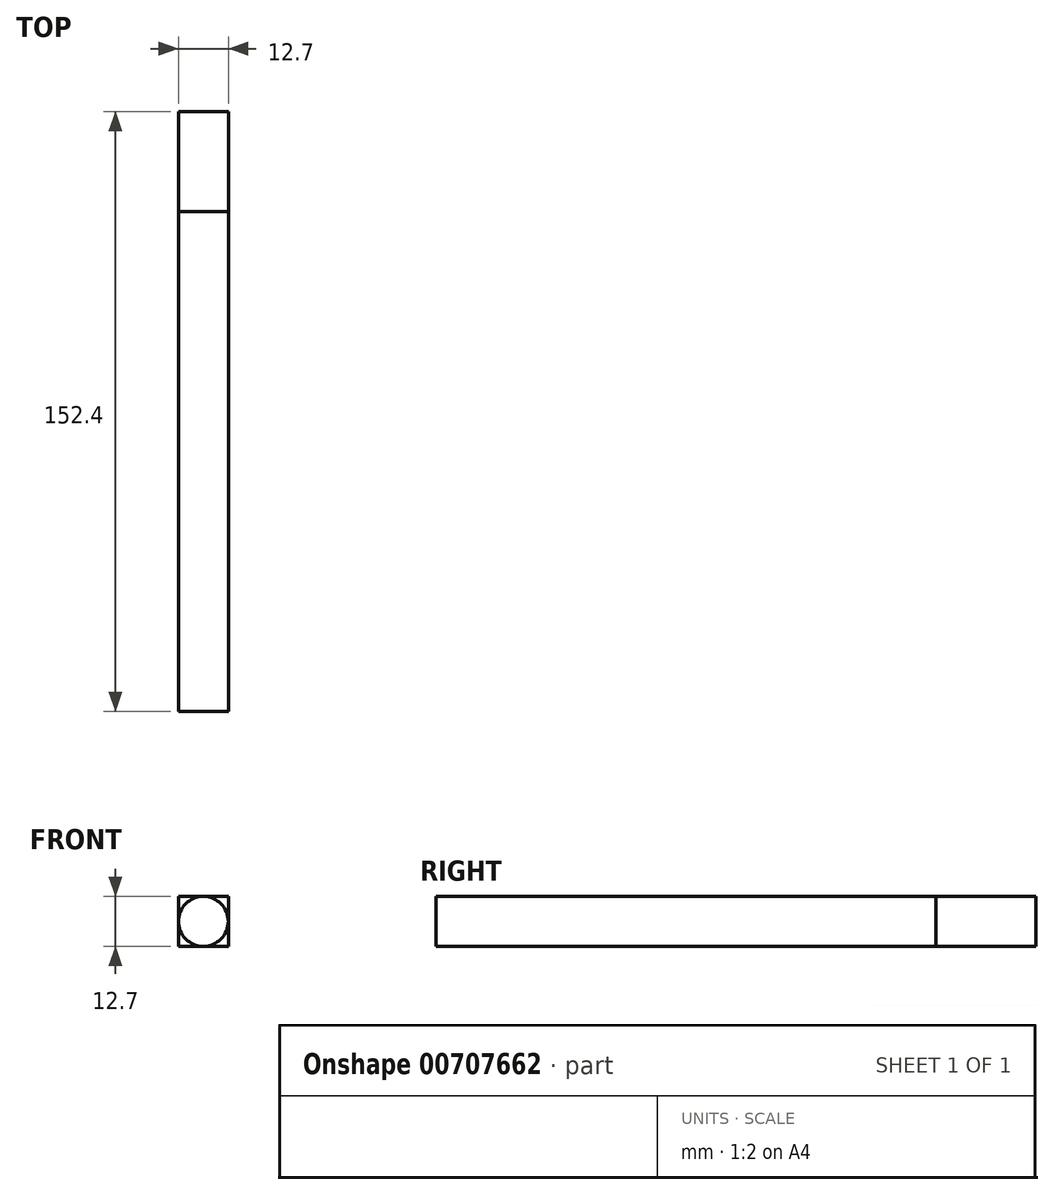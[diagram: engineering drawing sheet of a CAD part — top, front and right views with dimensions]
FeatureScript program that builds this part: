
annotation { "Feature Type Name" : "Feature", "Feature Type Description" : "" }
export const myFeature = defineFeature(function(context is Context, id is Id, definition is map)
    precondition{}
    {
        {
            var Q0;
            Q0=qCreatedBy(makeId("Front.planeOp"),FACE);
            var sketch = newSketch(context, id + "F0", { "sketchPlane" : qUnion([Q0])});
            skLineSegment(sketch, "E0.bottom", {"start": v(-6.35, 6.35) * mm, "end": v(6.35, 6.35) * mm});
            skLineSegment(sketch, "E0.top", {"start": v(-6.35, -6.35) * mm, "end": v(6.35, -6.35) * mm});
            skLineSegment(sketch, "E0.left", {"start": v(-6.35, 6.35) * mm, "end": v(-6.35, -6.35) * mm});
            skLineSegment(sketch, "E0.right", {"start": v(6.35, 6.35) * mm, "end": v(6.35, -6.35) * mm});
            skSolve(sketch);
        }
        {
            var Q0;
            Q0=makeQuery(id+"F0.imprint","IMPRINT",FACE,{"disambiguationData":[TD([[makeQuery(id+"F0.imprint","IMPRINT",EDGE,{"derivedFrom":sQuery(id+"F0.wireOp",EDGE,"E0.bottom")}),-1.0]])]});
            extrude(context, id + "F1", {"entities" : qUnion([Q0]), "depth" : 25.4 * mm, "offsetDistance" : 25.4 * mm});
        }
        {
            var Q0;
            Q0=makeQuery(id+"F1.opExtrude","CAP_FACE",FACE,{"disambiguationData":[OSD([sQuery(id+"F0.wireOp",EDGE,"E0.bottom"),sQuery(id+"F0.wireOp",EDGE,"E0.top"),sQuery(id+"F0.wireOp",EDGE,"E0.left"),sQuery(id+"F0.wireOp",EDGE,"E0.right")])],"isStart":false});
            var sketch = newSketch(context, id + "F2", { "sketchPlane" : qUnion([Q0])});
            skCircle(sketch, "E1", {"center": v(0, 0) * mm, "radius": 6.35 * mm});
            skSolve(sketch);
        }
        {
            var Q0;
            Q0 = qSketchRegion(id + "F2", true);
            extrude(context, id + "F3", {"entities" : qUnion([Q0]), "operationType" : NewBodyOperationType.ADD, "depth" : 127 * mm, "offsetDistance" : 25.4 * mm});
        }
    });
